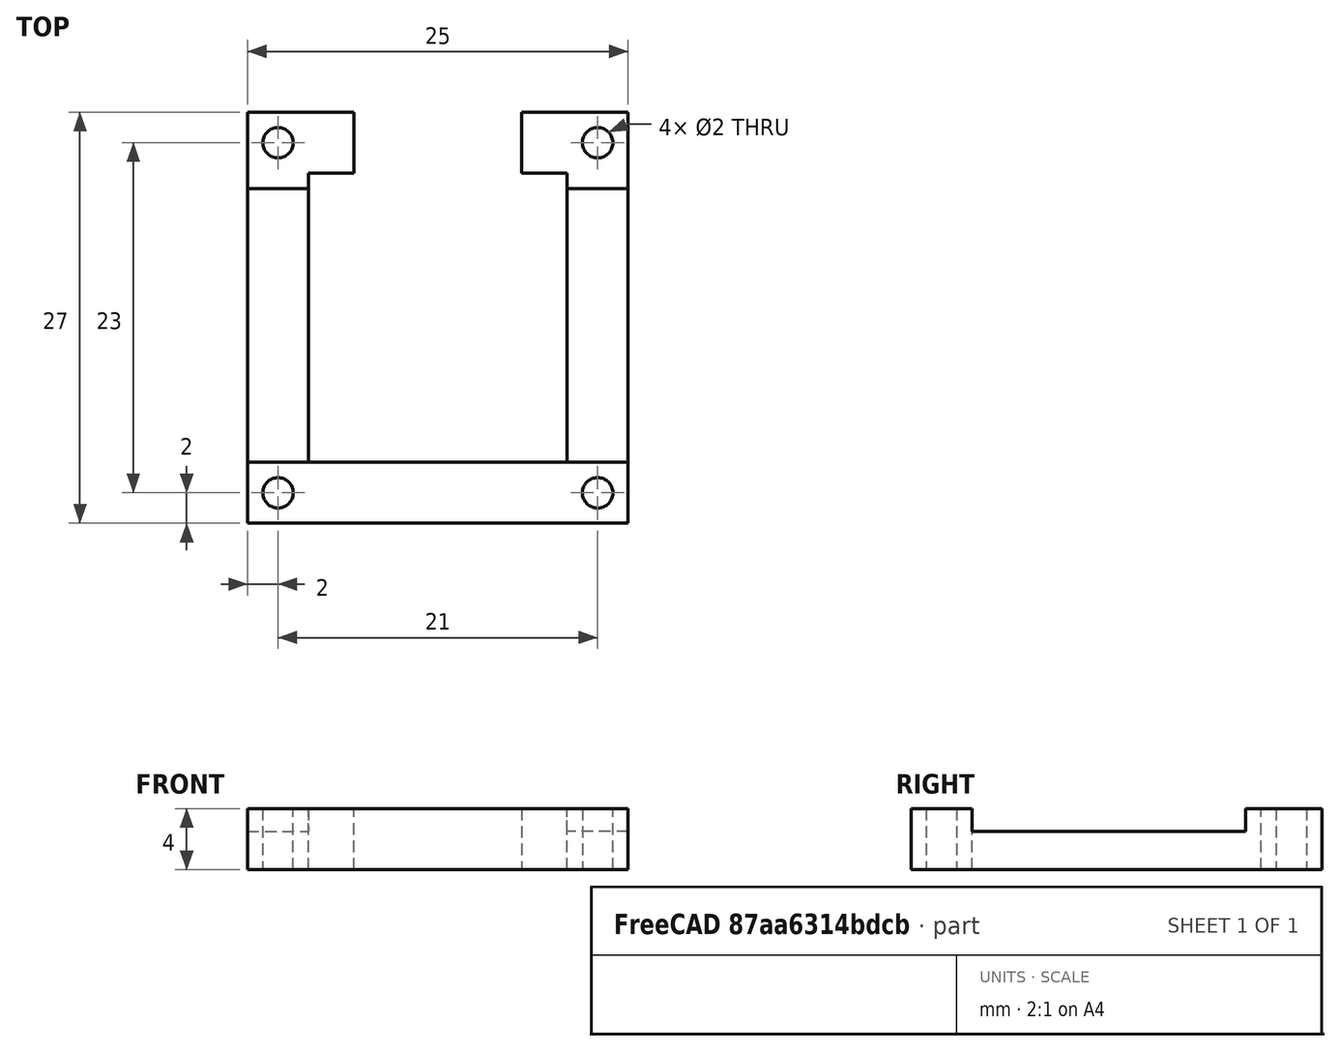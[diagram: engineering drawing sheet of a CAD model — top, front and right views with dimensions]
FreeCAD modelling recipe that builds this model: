
FCSTD DOCUMENT  (FreeCAD 0.19R24276 (Git))
Label: raiser
License: All rights reserved
LicenseURL: http://en.wikipedia.org/wiki/All_rights_reserved
objects: Part::Extrusion×9, Part::Part2DObjectPython×8, Part::Cut×8, App::DocumentObjectGroup×1
note: 25 computed .brp shape members not serialized (recipe doc carries the construction recipe); baked Part::Feature solids carry a one-line shape summary decoded from their .brp

FEATURE [Part::Part2DObjectPython] Rectangle  label="outer"  # Draft 2D object (typed FeaturePython)
  ChamferSize = 0
  Columns = 1
  FilletRadius = 0
  Height = 27
  Length = 25
  MakeFace = false
  Rows = 1
FEATURE [Part::Part2DObjectPython] Rectangle001  label="inner"  # Draft 2D object (typed FeaturePython)
  ChamferSize = 0
  Columns = 1
  FilletRadius = 0
  Height = 19
  Length = 17
  MakeFace = false
  Placement = pos=(4,4,0) rot=(0,0,1;0rad)
  Rows = 1
FEATURE [Part::Part2DObjectPython] Circle  label="TL"  # Draft 2D object (typed FeaturePython)
  FirstAngle = 0
  LastAngle = 0
  MakeFace = false
  Placement = pos=(2,25,0) rot=(0,0,1;0rad)
  Radius = 1
FEATURE [Part::Part2DObjectPython] Circle001  label="TR"  # Draft 2D object (typed FeaturePython)
  FirstAngle = 0
  LastAngle = 0
  MakeFace = false
  Placement = pos=(23,25,0) rot=(0,0,1;0rad)
  Radius = 1
FEATURE [Part::Part2DObjectPython] Circle002  label="BL"  # Draft 2D object (typed FeaturePython)
  FirstAngle = 0
  LastAngle = 0
  MakeFace = false
  Placement = pos=(2,2,0) rot=(0,0,1;0rad)
  Radius = 1
FEATURE [Part::Part2DObjectPython] Circle003  label="BR"  # Draft 2D object (typed FeaturePython)
  FirstAngle = 0
  LastAngle = 0
  MakeFace = false
  Placement = pos=(23,2,0) rot=(0,0,1;0rad)
  Radius = 1
FEATURE [Part::Extrusion] Extrude  label="Extrude outer"
  Base = -> Rectangle
  Dir = (0,0,1)
  DirMode = 2
  FaceMakerClass = Part::FaceMakerBullseye
  LengthFwd = 11
  LengthRev = 0
  Solid = true
  Symmetric = false
FEATURE [Part::Extrusion] Extrude001  label="Extrude inner"
  Base = -> Rectangle001
  Dir = (0,0,1)
  DirMode = 2
  FaceMakerClass = Part::FaceMakerBullseye
  LengthFwd = 11
  LengthRev = 0
  Solid = true
  Symmetric = false
FEATURE [Part::Extrusion] Extrude002  label="Extrude TL"
  Base = -> Circle
  Dir = (0,0,1)
  DirMode = 2
  FaceMakerClass = Part::FaceMakerBullseye
  LengthFwd = 11
  LengthRev = 0
  Solid = true
  Symmetric = false
FEATURE [Part::Extrusion] Extrude003  label="Extrude TR"
  Base = -> Circle001
  Dir = (0,0,1)
  DirMode = 2
  FaceMakerClass = Part::FaceMakerBullseye
  LengthFwd = 11
  LengthRev = 0
  Solid = true
  Symmetric = false
FEATURE [Part::Extrusion] Extrude004  label="Extrude BL"
  Base = -> Circle002
  Dir = (0,0,1)
  DirMode = 2
  FaceMakerClass = Part::FaceMakerBullseye
  LengthFwd = 11
  LengthRev = 0
  Solid = true
  Symmetric = false
FEATURE [Part::Extrusion] Extrude005  label="Extrude BR"
  Base = -> Circle003
  Dir = (0,0,1)
  DirMode = 2
  FaceMakerClass = Part::FaceMakerBullseye
  LengthFwd = 11
  LengthRev = 0
  Solid = true
  Symmetric = false
FEATURE [Part::Cut] Cut
  Base = -> Extrude
  Tool = -> Extrude001
FEATURE [Part::Cut] Cut001
  Base = -> Cut
  Tool = -> Extrude002
FEATURE [Part::Cut] Cut002
  Base = -> Cut001
  Tool = -> Extrude003
FEATURE [Part::Cut] Cut003
  Base = -> Cut002
  Tool = -> Extrude005
FEATURE [Part::Cut] Cut004
  Base = -> Cut003
  Tool = -> Extrude004
FEATURE [Part::Part2DObjectPython] Rectangle002  label="cutout"  # Draft 2D object (typed FeaturePython)
  ChamferSize = 0
  Columns = 1
  FilletRadius = 0
  Height = 5
  Length = 11
  MakeFace = false
  Placement = pos=(7,22,0) rot=(0,0,1;0rad)
  Rows = 1
FEATURE [Part::Extrusion] Extrude006
  Base = -> Rectangle002
  Dir = (0,0,1)
  DirMode = 2
  FaceMakerClass = Part::FaceMakerBullseye
  LengthFwd = 11
  LengthRev = 0
  Solid = true
  Symmetric = false
FEATURE [Part::Cut] Cut005
  Base = -> Cut004
  Tool = -> Extrude006
FEATURE [Part::Part2DObjectPython] Rectangle003  label="lower"  # Draft 2D object (typed FeaturePython)
  ChamferSize = 0
  Columns = 1
  FilletRadius = 0
  Height = 18
  Length = 26
  MakeFace = false
  Placement = pos=(0,4,9.5) rot=(0,0,1;0rad)
  Rows = 1
FEATURE [App::DocumentObjectGroup] Group  label="sketch"
  Group = -> [Circle,Circle001,Circle003,Circle002,Rectangle002,Rectangle003,Rectangle001,Rectangle]
FEATURE [Part::Extrusion] Extrude007
  Base = -> Rectangle003
  Dir = (0,0,1)
  DirMode = 2
  FaceMakerClass = Part::FaceMakerBullseye
  LengthFwd = 1.5
  LengthRev = 0
  Solid = true
  Symmetric = false
FEATURE [Part::Cut] Cut006
  Base = -> Cut005
  Tool = -> Extrude007
FEATURE [Part::Extrusion] Extrude008  label="smaller"
  Base = -> Rectangle
  Dir = (0,0,1)
  DirMode = 2
  FaceMakerClass = Part::FaceMakerBullseye
  LengthFwd = 7
  LengthRev = 0
  Solid = true
  Symmetric = false
FEATURE [Part::Cut] Cut007
  Base = -> Cut006
  Tool = -> Extrude008
